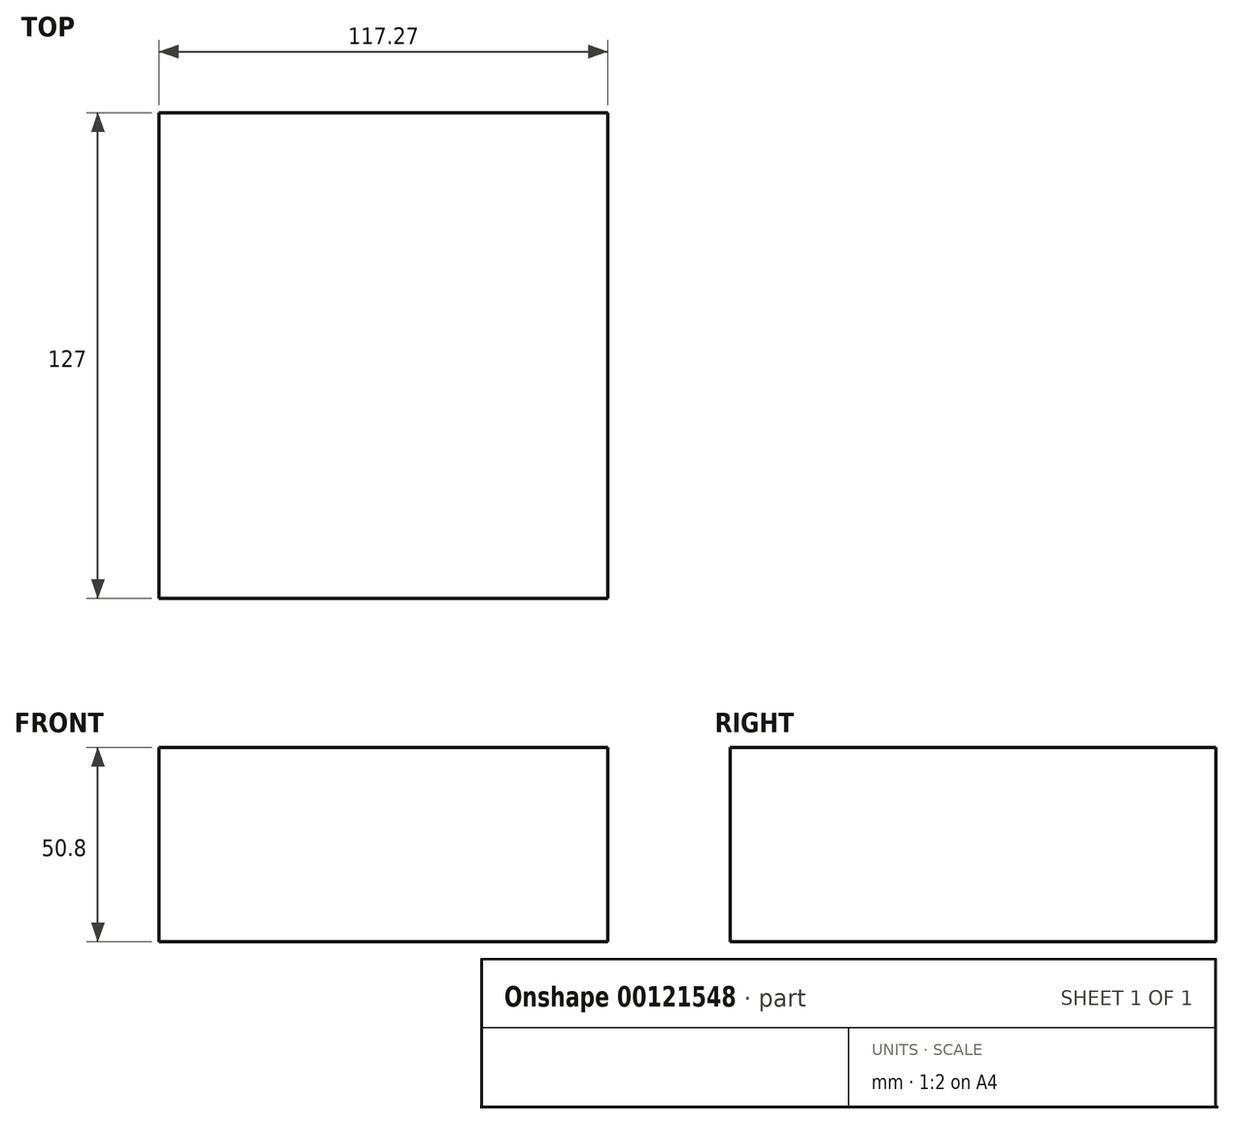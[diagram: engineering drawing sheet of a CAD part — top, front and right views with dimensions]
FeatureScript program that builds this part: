
annotation { "Feature Type Name" : "Feature", "Feature Type Description" : "" }
export const myFeature = defineFeature(function(context is Context, id is Id, definition is map)
    precondition{}
    {
        {
            var Q0;
            Q0=qCreatedBy(makeId("Top.planeOp"),FACE);
            var sketch = newSketch(context, id + "F0", { "sketchPlane" : qUnion([Q0])});
            skLineSegment(sketch, "E0.bottom", {"start": v(-62.71, -46.25) * mm, "end": v(54.56, -46.25) * mm});
            skLineSegment(sketch, "E0.top", {"start": v(-62.71, 80.75) * mm, "end": v(54.56, 80.75) * mm});
            skLineSegment(sketch, "E0.left", {"start": v(-62.71, -46.25) * mm, "end": v(-62.71, 80.75) * mm});
            skLineSegment(sketch, "E0.right", {"start": v(54.56, -46.25) * mm, "end": v(54.56, 80.75) * mm});
            skSolve(sketch);
        }
        {
            var Q0;
            Q0 = qSketchRegion(id + "F0", true);
            extrude(context, id + "F1", {"entities" : qUnion([Q0]), "depth" : 50.8 * mm});
        }
    });
